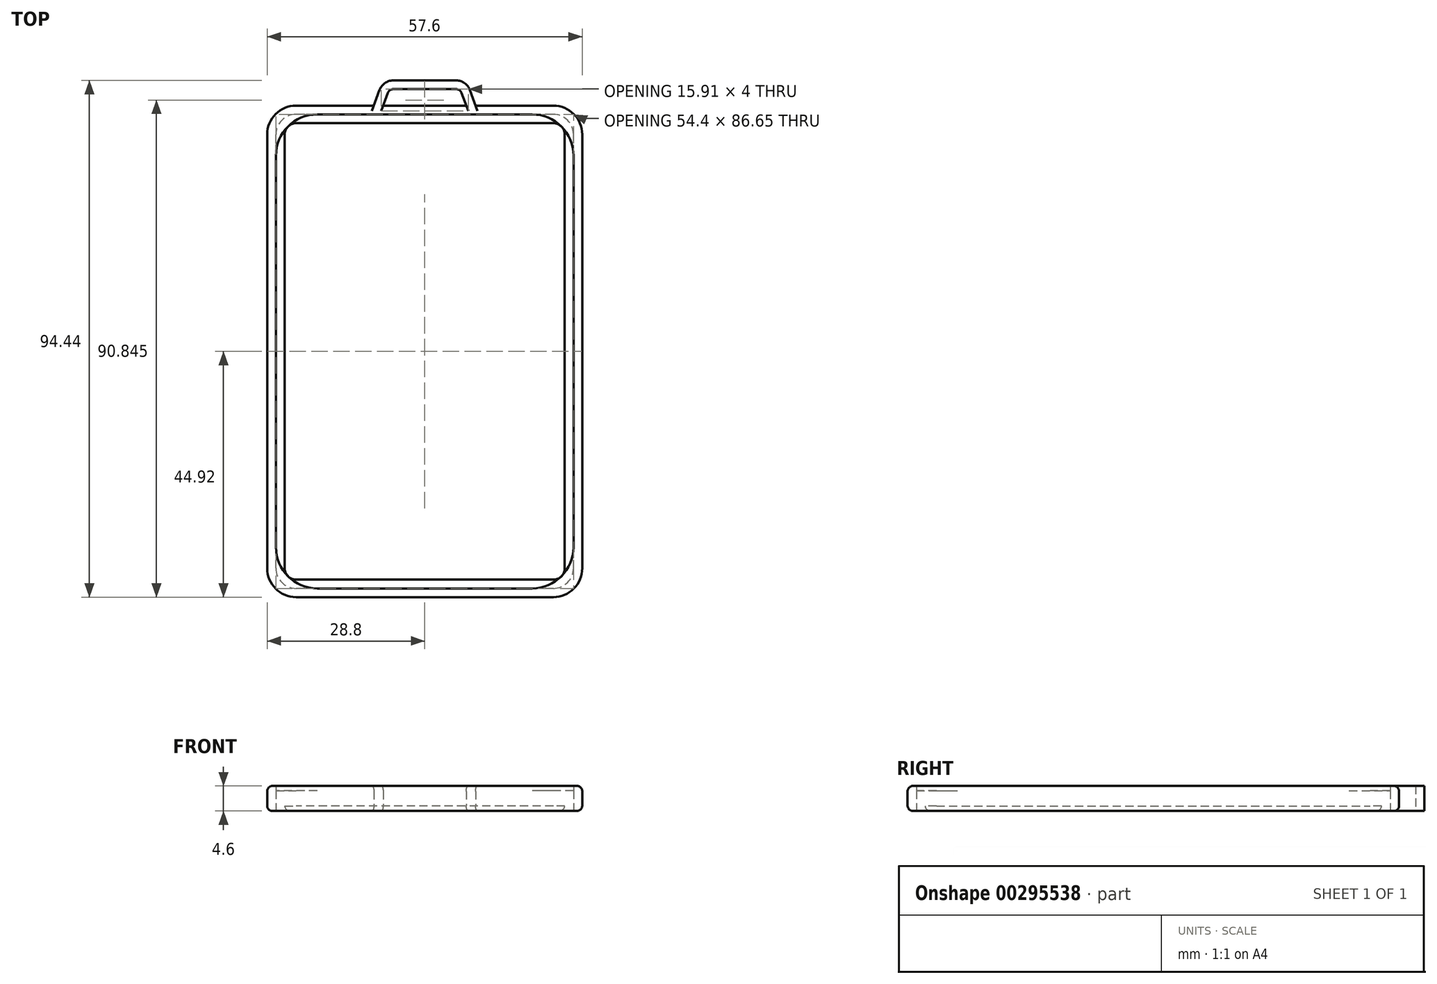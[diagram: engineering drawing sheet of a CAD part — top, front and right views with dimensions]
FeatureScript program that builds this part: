
annotation { "Feature Type Name" : "Feature", "Feature Type Description" : "" }
export const myFeature = defineFeature(function(context is Context, id is Id, definition is map)
    precondition{}
    {
        {
            assignVariable(context, id + "F0", {"variableType" : VariableType.LENGTH, "name" : "BadgeThickness", "lengthValue" : 2.8 * mm});
        }
        {
            var Q0;
            Q0=qCreatedBy(makeId("Top.planeOp"),FACE);
            var sketch = newSketch(context, id + "F1", { "sketchPlane" : qUnion([Q0])});
            skLineSegment(sketch, "E0.bottom", {"start": v(23.52, -43.13) * mm, "end": v(-23.51, -43.13) * mm});
            skLineSegment(sketch, "E0.top", {"start": v(23.51, 43.13) * mm, "end": v(-23.52, 43.13) * mm});
            skLineSegment(sketch, "E0.left", {"start": v(27, -39.64) * mm, "end": v(27, 39.64) * mm});
            skLineSegment(sketch, "E0.right", {"start": v(-27, -39.64) * mm, "end": v(-27, 39.64) * mm, "construction": true});
            skPoint(sketch, "E0.middle", {"position": v(0, 0) * mm});
            skPoint(sketch, "E1.visualSharp", {"position": v(-27, 43.13) * mm});
            skArc(sketch, "E1.filletArc", {"start": v(-23.52, 43.13) * mm, "mid": v(-25.98, 42.1) * mm, "end": v(-27, 39.64) * mm});
            skPoint(sketch, "E2.visualSharp", {"position": v(27, 43.13) * mm});
            skArc(sketch, "E2.filletArc", {"start": v(27, 39.64) * mm, "mid": v(25.98, 42.1) * mm, "end": v(23.51, 43.12) * mm});
            skPoint(sketch, "E3.visualSharp", {"position": v(27, -43.12) * mm});
            skArc(sketch, "E3.filletArc", {"start": v(23.52, -43.12) * mm, "mid": v(25.98, -42.1) * mm, "end": v(27, -39.64) * mm});
            skPoint(sketch, "E4.visualSharp", {"position": v(-27, -43.13) * mm});
            skArc(sketch, "E4.filletArc", {"start": v(-27, -39.64) * mm, "mid": v(-25.98, -42.1) * mm, "end": v(-23.51, -43.13) * mm});
            skArc(sketch, "E5.0", {"start": v(-27.2, -39.64) * mm, "mid": v(-26.12, -42.25) * mm, "end": v(-23.51, -43.33) * mm});
            skLineSegment(sketch, "E5.1", {"start": v(23.52, -43.33) * mm, "end": v(-23.51, -43.33) * mm});
            skLineSegment(sketch, "E5.2", {"start": v(-27.2, -39.64) * mm, "end": v(-27.2, 39.64) * mm});
            skArc(sketch, "E5.3", {"start": v(23.52, -43.32) * mm, "mid": v(26.12, -42.25) * mm, "end": v(27.2, -39.64) * mm});
            skArc(sketch, "E5.4", {"start": v(-23.52, 43.33) * mm, "mid": v(-26.12, 42.25) * mm, "end": v(-27.2, 39.64) * mm});
            skLineSegment(sketch, "E5.5", {"start": v(23.51, 43.33) * mm, "end": v(-23.52, 43.33) * mm});
            skArc(sketch, "E5.6", {"start": v(27.2, 39.64) * mm, "mid": v(26.12, 42.25) * mm, "end": v(23.51, 43.32) * mm});
            skLineSegment(sketch, "E5.7", {"start": v(27.2, -39.64) * mm, "end": v(27.2, 39.64) * mm});
            skArc(sketch, "E6.0", {"start": v(-28.8, -39.64) * mm, "mid": v(-27.25, -43.38) * mm, "end": v(-23.51, -44.92) * mm});
            skLineSegment(sketch, "E6.1", {"start": v(23.52, -44.93) * mm, "end": v(-23.51, -44.93) * mm});
            skLineSegment(sketch, "E6.2", {"start": v(-28.8, -39.64) * mm, "end": v(-28.8, 39.64) * mm});
            skArc(sketch, "E6.3", {"start": v(23.52, -44.92) * mm, "mid": v(27.25, -43.38) * mm, "end": v(28.8, -39.64) * mm});
            skArc(sketch, "E6.4", {"start": v(-23.52, 44.92) * mm, "mid": v(-27.25, 43.38) * mm, "end": v(-28.8, 39.64) * mm});
            skLineSegment(sketch, "E6.5", {"start": v(23.51, 44.93) * mm, "end": v(-23.52, 44.93) * mm});
            skArc(sketch, "E6.6", {"start": v(28.8, 39.64) * mm, "mid": v(27.25, 43.38) * mm, "end": v(23.51, 44.92) * mm});
            skLineSegment(sketch, "E6.7", {"start": v(28.8, -39.64) * mm, "end": v(28.8, 39.64) * mm});
            skSolve(sketch);
        }
        {
            var Q0;
            Q0=makeQuery(id+"F1.imprint","IMPRINT",FACE,{"disambiguationData":[TD([[makeQuery(id+"F1.imprint","IMPRINT",EDGE,{"derivedFrom":sQuery(id+"F1.wireOp",EDGE,"E5.0")}),-1.0]])]});
            extrude(context, id + "F2", {"entities" : qUnion([Q0]), "offsetDistance" : 25 * mm, "depth" : getVariable(context, 'BadgeThickness')});
        }
        {
            var Q0;
            Q0=makeQuery(id+"F2.opExtrude","CAP_FACE",FACE,{"disambiguationData":[OSD([sQuery(id+"F1.wireOp",EDGE,"E5.0"),sQuery(id+"F1.wireOp",EDGE,"E5.1"),sQuery(id+"F1.wireOp",EDGE,"E5.2"),sQuery(id+"F1.wireOp",EDGE,"E5.3"),sQuery(id+"F1.wireOp",EDGE,"E5.4"),sQuery(id+"F1.wireOp",EDGE,"E5.5"),sQuery(id+"F1.wireOp",EDGE,"E5.6"),sQuery(id+"F1.wireOp",EDGE,"E5.7"),sQuery(id+"F1.wireOp",EDGE,"E6.0"),sQuery(id+"F1.wireOp",EDGE,"E6.1"),sQuery(id+"F1.wireOp",EDGE,"E6.2"),sQuery(id+"F1.wireOp",EDGE,"E6.3"),sQuery(id+"F1.wireOp",EDGE,"E6.4"),sQuery(id+"F1.wireOp",EDGE,"E6.5"),sQuery(id+"F1.wireOp",EDGE,"E6.6"),sQuery(id+"F1.wireOp",EDGE,"E6.7")])],"isStart":true});
            var sketch = newSketch(context, id + "F3", { "sketchPlane" : qUnion([Q0])});
            skArc(sketch, "E7.0.0", {"start": v(28.8, 39.64) * mm, "mid": v(27.25, 43.38) * mm, "end": v(23.52, 44.92) * mm});
            skLineSegment(sketch, "E7.0.1", {"start": v(23.52, 44.93) * mm, "end": v(-23.51, 44.93) * mm});
            skArc(sketch, "E7.0.2", {"start": v(-23.51, 44.93) * mm, "mid": v(-27.25, 43.38) * mm, "end": v(-28.8, 39.64) * mm});
            skLineSegment(sketch, "E7.0.3", {"start": v(-28.8, 39.64) * mm, "end": v(-28.8, -39.64) * mm});
            skArc(sketch, "E7.0.4", {"start": v(-28.8, -39.64) * mm, "mid": v(-27.25, -43.38) * mm, "end": v(-23.52, -44.93) * mm});
            skLineSegment(sketch, "E7.0.5", {"start": v(-23.52, -44.93) * mm, "end": v(23.51, -44.93) * mm});
            skArc(sketch, "E7.0.6", {"start": v(23.51, -44.92) * mm, "mid": v(27.25, -43.38) * mm, "end": v(28.8, -39.64) * mm});
            skLineSegment(sketch, "E7.0.7", {"start": v(28.8, -39.64) * mm, "end": v(28.8, 39.64) * mm});
            skArc(sketch, "E8.0", {"start": v(-25.6, 39.64) * mm, "mid": v(-24.99, 41.11) * mm, "end": v(-23.51, 41.73) * mm});
            skLineSegment(sketch, "E8.1", {"start": v(23.51, 41.73) * mm, "end": v(-23.51, 41.73) * mm});
            skLineSegment(sketch, "E8.2", {"start": v(-25.6, 39.64) * mm, "end": v(-25.6, -39.64) * mm});
            skArc(sketch, "E8.3", {"start": v(23.51, 41.72) * mm, "mid": v(24.99, 41.11) * mm, "end": v(25.6, 39.64) * mm});
            skArc(sketch, "E8.4", {"start": v(-23.52, -41.73) * mm, "mid": v(-24.99, -41.11) * mm, "end": v(-25.6, -39.64) * mm});
            skLineSegment(sketch, "E8.5", {"start": v(23.51, -41.73) * mm, "end": v(-23.52, -41.73) * mm});
            skArc(sketch, "E8.6", {"start": v(25.6, -39.64) * mm, "mid": v(24.99, -41.11) * mm, "end": v(23.51, -41.73) * mm});
            skLineSegment(sketch, "E8.7", {"start": v(25.6, 39.64) * mm, "end": v(25.6, -39.64) * mm});
            skSolve(sketch);
        }
        {
            var Q0;
            Q0=makeQuery(id+"F3.imprint","IMPRINT",FACE,{"disambiguationData":[TD([[makeQuery(id+"F3.imprint","IMPRINT",EDGE,{"derivedFrom":sQuery(id+"F3.wireOp",EDGE,"E8.0")}),1.0]])]});
            var Q1;
            Q1=makeQuery(id+"F3.imprint","IMPRINT",FACE,{"disambiguationData":[TD([[makeQuery(id+"F3.imprint","IMPRINT",EDGE,{"derivedFrom":sQuery(id+"F3.wireOp",EDGE,"E7.0.0")}),-1.0]])]});
            extrude(context, id + "F4", {"entities" : qUnion([Q0, Q1]), "operationType" : NewBodyOperationType.ADD, "depth" : 0.9 * mm});
        }
        {
            var Q0;
            Q0=makeQuery(id+"F2.opExtrude","CAP_FACE",FACE,{"disambiguationData":[OSD([sQuery(id+"F1.wireOp",EDGE,"E5.0"),sQuery(id+"F1.wireOp",EDGE,"E5.1"),sQuery(id+"F1.wireOp",EDGE,"E5.2"),sQuery(id+"F1.wireOp",EDGE,"E5.3"),sQuery(id+"F1.wireOp",EDGE,"E5.4"),sQuery(id+"F1.wireOp",EDGE,"E5.5"),sQuery(id+"F1.wireOp",EDGE,"E5.6"),sQuery(id+"F1.wireOp",EDGE,"E5.7"),sQuery(id+"F1.wireOp",EDGE,"E6.0"),sQuery(id+"F1.wireOp",EDGE,"E6.1"),sQuery(id+"F1.wireOp",EDGE,"E6.2"),sQuery(id+"F1.wireOp",EDGE,"E6.3"),sQuery(id+"F1.wireOp",EDGE,"E6.4"),sQuery(id+"F1.wireOp",EDGE,"E6.5"),sQuery(id+"F1.wireOp",EDGE,"E6.6"),sQuery(id+"F1.wireOp",EDGE,"E6.7")])],"isStart":false});
            var sketch = newSketch(context, id + "F5", { "sketchPlane" : qUnion([Q0])});
            skLineSegment(sketch, "E9.0", {"start": v(23.51, 43.33) * mm, "end": v(-23.52, 43.33) * mm});
            skLineSegment(sketch, "E10.0", {"start": v(-27.2, -39.64) * mm, "end": v(-27.2, 39.64) * mm});
            skLineSegment(sketch, "E11.0", {"start": v(27.2, -39.64) * mm, "end": v(27.2, 39.64) * mm});
            skLineSegment(sketch, "E12.0", {"start": v(23.52, -43.33) * mm, "end": v(-23.51, -43.33) * mm});
            skArc(sketch, "E13", {"start": v(-27.2, -35.78) * mm, "mid": v(-24.99, -41.11) * mm, "end": v(-19.65, -43.33) * mm});
            skArc(sketch, "E14", {"start": v(19.65, -43.33) * mm, "mid": v(24.99, -41.11) * mm, "end": v(27.2, -35.78) * mm});
            skArc(sketch, "E15", {"start": v(27.2, 35.78) * mm, "mid": v(24.99, 41.11) * mm, "end": v(19.65, 43.33) * mm});
            skArc(sketch, "E16", {"start": v(-19.65, 43.33) * mm, "mid": v(-24.99, 41.11) * mm, "end": v(-27.2, 35.78) * mm});
            skArc(sketch, "E17.0.0", {"start": v(23.52, -44.92) * mm, "mid": v(27.25, -43.38) * mm, "end": v(28.8, -39.64) * mm});
            skLineSegment(sketch, "E17.0.1", {"start": v(28.8, -39.64) * mm, "end": v(28.8, 39.64) * mm});
            skArc(sketch, "E17.0.2", {"start": v(28.8, 39.64) * mm, "mid": v(27.25, 43.38) * mm, "end": v(23.51, 44.92) * mm});
            skLineSegment(sketch, "E17.0.3", {"start": v(23.51, 44.93) * mm, "end": v(-23.52, 44.93) * mm});
            skArc(sketch, "E17.0.4", {"start": v(-23.52, 44.93) * mm, "mid": v(-27.25, 43.38) * mm, "end": v(-28.8, 39.64) * mm});
            skLineSegment(sketch, "E17.0.5", {"start": v(-28.8, 39.64) * mm, "end": v(-28.8, -39.64) * mm});
            skArc(sketch, "E17.0.6", {"start": v(-28.8, -39.64) * mm, "mid": v(-27.25, -43.38) * mm, "end": v(-23.51, -44.93) * mm});
            skLineSegment(sketch, "E17.0.7", {"start": v(-23.51, -44.93) * mm, "end": v(23.52, -44.93) * mm});
            skSolve(sketch);
        }
        {
            var Q0;
            Q0=makeQuery(id+"F5.imprint","IMPRINT",FACE,{"disambiguationData":[TD([[makeQuery(id+"F5.imprint","IMPRINT",EDGE,{"derivedFrom":sQuery(id+"F5.wireOp",EDGE,"E17.0.0")}),1.0]])]});
            var Q1;
            {var subQ2=sQuery(id+"F5.wireOp",EDGE,"E16");Q1=makeQuery(id+"F5.imprint","IMPRINT",FACE,{"disambiguationData":[TD([[makeQuery(id+"F5.imprint","IMPRINT",EDGE,{"derivedFrom":subQ2}),-1.0]])]});}
            var Q2;
            {var subQ2=sQuery(id+"F5.wireOp",EDGE,"E15");Q2=makeQuery(id+"F5.imprint","IMPRINT",FACE,{"disambiguationData":[TD([[makeQuery(id+"F5.imprint","IMPRINT",EDGE,{"derivedFrom":subQ2}),-1.0]])]});}
            var Q3;
            {var subQ2=sQuery(id+"F5.wireOp",EDGE,"E14");Q3=makeQuery(id+"F5.imprint","IMPRINT",FACE,{"disambiguationData":[TD([[makeQuery(id+"F5.imprint","IMPRINT",EDGE,{"derivedFrom":subQ2}),-1.0]])]});}
            var Q4;
            {var subQ2=sQuery(id+"F5.wireOp",EDGE,"E13");Q4=makeQuery(id+"F5.imprint","IMPRINT",FACE,{"disambiguationData":[TD([[makeQuery(id+"F5.imprint","IMPRINT",EDGE,{"derivedFrom":subQ2}),-1.0]])]});}
            extrude(context, id + "F6", {"entities" : qUnion([Q0, Q1, Q2, Q3, Q4]), "operationType" : NewBodyOperationType.ADD, "depth" : 0.9 * mm});
        }
        {
            var Q0;
            Q0=qCreatedBy(makeId("Top.planeOp"),FACE);
            var sketch = newSketch(context, id + "F7", { "sketchPlane" : qUnion([Q0])});
            skLineSegment(sketch, "E18", {"start": v(-7.6, 44.93) * mm, "end": v(-6.74, 47.27) * mm});
            skLineSegment(sketch, "E19", {"start": v(-5.8, 47.93) * mm, "end": v(5.8, 47.93) * mm});
            skLineSegment(sketch, "E20", {"start": v(6.74, 47.27) * mm, "end": v(7.6, 44.93) * mm});
            skLineSegment(sketch, "E21", {"start": v(0, 0) * mm, "end": v(0, 7.2) * mm, "construction": true});
            skPoint(sketch, "E22.visualSharp", {"position": v(-6.5, 47.93) * mm});
            skArc(sketch, "E22.filletArc", {"start": v(-5.8, 47.93) * mm, "mid": v(-6.37, 47.74) * mm, "end": v(-6.74, 47.27) * mm});
            skPoint(sketch, "E23.visualSharp", {"position": v(6.5, 47.93) * mm});
            skArc(sketch, "E23.filletArc", {"start": v(6.74, 47.27) * mm, "mid": v(6.37, 47.74) * mm, "end": v(5.8, 47.93) * mm});
            skLineSegment(sketch, "E24.0", {"start": v(8.24, 47.81) * mm, "end": v(9.3, 44.93) * mm});
            skLineSegment(sketch, "E24.1", {"start": v(-9.3, 44.93) * mm, "end": v(-8.24, 47.81) * mm});
            skArc(sketch, "E24.2", {"start": v(-5.8, 49.53) * mm, "mid": v(-7.3, 49.05) * mm, "end": v(-8.24, 47.81) * mm});
            skLineSegment(sketch, "E24.3", {"start": v(-5.8, 49.53) * mm, "end": v(5.8, 49.53) * mm});
            skArc(sketch, "E24.4", {"start": v(8.24, 47.81) * mm, "mid": v(7.3, 49.05) * mm, "end": v(5.8, 49.53) * mm});
            skLineSegment(sketch, "E25", {"start": v(9.3, 44.93) * mm, "end": v(7.6, 44.93) * mm});
            skLineSegment(sketch, "E26", {"start": v(-7.6, 44.93) * mm, "end": v(-9.3, 44.93) * mm});
            skSolve(sketch);
        }
        {
            var Q0;
            Q0 = qSketchRegion(id + "F7", true);
            var Q1;
            Q1=makeQuery(id+"F6.opExtrude","CAP_FACE",FACE,{"disambiguationData":[OSD([sQuery(id+"F5.wireOp",EDGE,"E9.0"),sQuery(id+"F5.wireOp",EDGE,"E10.0"),sQuery(id+"F5.wireOp",EDGE,"E11.0"),sQuery(id+"F5.wireOp",EDGE,"E12.0"),sQuery(id+"F5.wireOp",EDGE,"E13"),sQuery(id+"F5.wireOp",EDGE,"E14"),sQuery(id+"F5.wireOp",EDGE,"E15"),sQuery(id+"F5.wireOp",EDGE,"E16"),sQuery(id+"F5.wireOp",EDGE,"E17.0.0"),sQuery(id+"F5.wireOp",EDGE,"E17.0.1"),sQuery(id+"F5.wireOp",EDGE,"E17.0.2"),sQuery(id+"F5.wireOp",EDGE,"E17.0.3"),sQuery(id+"F5.wireOp",EDGE,"E17.0.4"),sQuery(id+"F5.wireOp",EDGE,"E17.0.5"),sQuery(id+"F5.wireOp",EDGE,"E17.0.6"),sQuery(id+"F5.wireOp",EDGE,"E17.0.7")])],"isStart":false});
            var Q2;
            Q2=makeQuery(id+"F4.opExtrude","CAP_FACE",FACE,{"disambiguationData":[OSD([sQuery(id+"F3.wireOp",EDGE,"E7.0.0"),sQuery(id+"F3.wireOp",EDGE,"E7.0.1"),sQuery(id+"F3.wireOp",EDGE,"E7.0.2"),sQuery(id+"F3.wireOp",EDGE,"E7.0.3"),sQuery(id+"F3.wireOp",EDGE,"E7.0.4"),sQuery(id+"F3.wireOp",EDGE,"E7.0.5"),sQuery(id+"F3.wireOp",EDGE,"E7.0.6"),sQuery(id+"F3.wireOp",EDGE,"E7.0.7"),sQuery(id+"F3.wireOp",EDGE,"E8.0"),sQuery(id+"F3.wireOp",EDGE,"E8.1"),sQuery(id+"F3.wireOp",EDGE,"E8.2"),sQuery(id+"F3.wireOp",EDGE,"E8.3"),sQuery(id+"F3.wireOp",EDGE,"E8.4"),sQuery(id+"F3.wireOp",EDGE,"E8.5"),sQuery(id+"F3.wireOp",EDGE,"E8.6"),sQuery(id+"F3.wireOp",EDGE,"E8.7")])],"isStart":false});
            extrude(context, id + "F8", {"entities" : qUnion([Q0]), "operationType" : NewBodyOperationType.ADD, "endBound" : BoundingType.UP_TO_SURFACE, "endBoundEntityFace" : qUnion([Q1]), "depth" : 25 * mm, "hasSecondDirection" : true, "secondDirectionBound" : SecondDirectionBoundingType.UP_TO_SURFACE, "secondDirectionOppositeDirection" : true, "secondDirectionBoundEntityFace" : qUnion([Q2]), "secondDirectionDepth" : 25 * mm});
        }
        {
            var Q0;
            Q0=makeQuery(id+"F6.opExtrude","CAP_EDGE",EDGE,{"disambiguationData":[OSD([sQuery(id+"F5.wireOp",EDGE,"E17.0.5")])],"isStart":false});
            var Q1;
            Q1=makeQuery(id+"F4.opExtrude","CAP_EDGE",EDGE,{"disambiguationData":[OSD([sQuery(id+"F3.wireOp",EDGE,"E7.0.3")])],"isStart":false});
            var Q2;
            Q2=makeQuery(id+"F8.opExtrude","TWEAK_EDGE",EDGE,{"derivedFrom":[makeQuery(id+"F6.opExtrude","CAP_FACE",FACE,{"disambiguationData":[OSD([sQuery(id+"F5.wireOp",EDGE,"E9.0"),sQuery(id+"F5.wireOp",EDGE,"E10.0"),sQuery(id+"F5.wireOp",EDGE,"E11.0"),sQuery(id+"F5.wireOp",EDGE,"E12.0"),sQuery(id+"F5.wireOp",EDGE,"E13"),sQuery(id+"F5.wireOp",EDGE,"E14"),sQuery(id+"F5.wireOp",EDGE,"E15"),sQuery(id+"F5.wireOp",EDGE,"E16"),sQuery(id+"F5.wireOp",EDGE,"E17.0.0"),sQuery(id+"F5.wireOp",EDGE,"E17.0.1"),sQuery(id+"F5.wireOp",EDGE,"E17.0.2"),sQuery(id+"F5.wireOp",EDGE,"E17.0.3"),sQuery(id+"F5.wireOp",EDGE,"E17.0.4"),sQuery(id+"F5.wireOp",EDGE,"E17.0.5"),sQuery(id+"F5.wireOp",EDGE,"E17.0.6"),sQuery(id+"F5.wireOp",EDGE,"E17.0.7")])],"isStart":false}),makeQuery(id+"F7.imprint","IMPRINT",EDGE,{"derivedFrom":sQuery(id+"F7.wireOp",EDGE,"E18")})]});
            var Q3;
            Q3=makeQuery(id+"F8.opExtrude","TWEAK_EDGE",EDGE,{"derivedFrom":[makeQuery(id+"F4.opExtrude","CAP_FACE",FACE,{"disambiguationData":[OSD([sQuery(id+"F3.wireOp",EDGE,"E7.0.0"),sQuery(id+"F3.wireOp",EDGE,"E7.0.1"),sQuery(id+"F3.wireOp",EDGE,"E7.0.2"),sQuery(id+"F3.wireOp",EDGE,"E7.0.3"),sQuery(id+"F3.wireOp",EDGE,"E7.0.4"),sQuery(id+"F3.wireOp",EDGE,"E7.0.5"),sQuery(id+"F3.wireOp",EDGE,"E7.0.6"),sQuery(id+"F3.wireOp",EDGE,"E7.0.7"),sQuery(id+"F3.wireOp",EDGE,"E8.0"),sQuery(id+"F3.wireOp",EDGE,"E8.1"),sQuery(id+"F3.wireOp",EDGE,"E8.2"),sQuery(id+"F3.wireOp",EDGE,"E8.3"),sQuery(id+"F3.wireOp",EDGE,"E8.4"),sQuery(id+"F3.wireOp",EDGE,"E8.5"),sQuery(id+"F3.wireOp",EDGE,"E8.6"),sQuery(id+"F3.wireOp",EDGE,"E8.7")])],"isStart":false}),makeQuery(id+"F7.imprint","IMPRINT",EDGE,{"derivedFrom":sQuery(id+"F7.wireOp",EDGE,"E24.3")})]});
            var Q4;
            Q4=makeQuery(id+"F8.opExtrude","TWEAK_EDGE",EDGE,{"derivedFrom":[makeQuery(id+"F6.opExtrude","CAP_FACE",FACE,{"disambiguationData":[OSD([sQuery(id+"F5.wireOp",EDGE,"E9.0"),sQuery(id+"F5.wireOp",EDGE,"E10.0"),sQuery(id+"F5.wireOp",EDGE,"E11.0"),sQuery(id+"F5.wireOp",EDGE,"E12.0"),sQuery(id+"F5.wireOp",EDGE,"E13"),sQuery(id+"F5.wireOp",EDGE,"E14"),sQuery(id+"F5.wireOp",EDGE,"E15"),sQuery(id+"F5.wireOp",EDGE,"E16"),sQuery(id+"F5.wireOp",EDGE,"E17.0.0"),sQuery(id+"F5.wireOp",EDGE,"E17.0.1"),sQuery(id+"F5.wireOp",EDGE,"E17.0.2"),sQuery(id+"F5.wireOp",EDGE,"E17.0.3"),sQuery(id+"F5.wireOp",EDGE,"E17.0.4"),sQuery(id+"F5.wireOp",EDGE,"E17.0.5"),sQuery(id+"F5.wireOp",EDGE,"E17.0.6"),sQuery(id+"F5.wireOp",EDGE,"E17.0.7")])],"isStart":false}),makeQuery(id+"F7.imprint","IMPRINT",EDGE,{"derivedFrom":sQuery(id+"F7.wireOp",EDGE,"E24.3")})]});
            var Q5;
            {var subQ0=sQuery(id+"F3.wireOp",EDGE,"E7.0.5");Q5=makeQuery(id+"F8.boolean.opBoolean","SPLIT",EDGE,{"disambiguationData":[TD([makeQuery(id+"F8.opExtrude","SWEPT_FACE",FACE,{"disambiguationData":[OSD([sQuery(id+"F7.wireOp",EDGE,"E18")])]})])],"derivedFrom":makeQuery(id+"F4.opExtrude","CAP_EDGE",EDGE,{"disambiguationData":[OSD([subQ0])],"isStart":false})});}
            var Q6;
            {var subQ4=sQuery(id+"F5.wireOp",EDGE,"E17.0.3");Q6=makeQuery(id+"F8.boolean.opBoolean","SPLIT",EDGE,{"disambiguationData":[TD([makeQuery(id+"F8.opExtrude","SWEPT_FACE",FACE,{"disambiguationData":[OSD([sQuery(id+"F7.wireOp",EDGE,"E18")])]})])],"derivedFrom":makeQuery(id+"F6.opExtrude","CAP_EDGE",EDGE,{"disambiguationData":[OSD([subQ4])],"isStart":false})});}
            var Q7;
            Q7=makeQuery(id+"F8.opExtrude","TWEAK_EDGE",EDGE,{"derivedFrom":[makeQuery(id+"F4.opExtrude","CAP_FACE",FACE,{"disambiguationData":[OSD([sQuery(id+"F3.wireOp",EDGE,"E7.0.0"),sQuery(id+"F3.wireOp",EDGE,"E7.0.1"),sQuery(id+"F3.wireOp",EDGE,"E7.0.2"),sQuery(id+"F3.wireOp",EDGE,"E7.0.3"),sQuery(id+"F3.wireOp",EDGE,"E7.0.4"),sQuery(id+"F3.wireOp",EDGE,"E7.0.5"),sQuery(id+"F3.wireOp",EDGE,"E7.0.6"),sQuery(id+"F3.wireOp",EDGE,"E7.0.7"),sQuery(id+"F3.wireOp",EDGE,"E8.0"),sQuery(id+"F3.wireOp",EDGE,"E8.1"),sQuery(id+"F3.wireOp",EDGE,"E8.2"),sQuery(id+"F3.wireOp",EDGE,"E8.3"),sQuery(id+"F3.wireOp",EDGE,"E8.4"),sQuery(id+"F3.wireOp",EDGE,"E8.5"),sQuery(id+"F3.wireOp",EDGE,"E8.6"),sQuery(id+"F3.wireOp",EDGE,"E8.7")])],"isStart":false}),makeQuery(id+"F7.imprint","IMPRINT",EDGE,{"derivedFrom":sQuery(id+"F7.wireOp",EDGE,"E19")})]});
            var Q8;
            Q8=makeQuery(id+"F4.opExtrude","CAP_EDGE",EDGE,{"disambiguationData":[OSD([sQuery(id+"F3.wireOp",EDGE,"E8.2")])],"isStart":false});
            fillet(context, id + "F9", {"entities" : qUnion([Q0, Q1, Q2, Q3, Q4, Q5, Q6, Q7, Q8]), "radius" : 1 * mm, "tangentPropagation" : true, "allowEdgeOverflow" : false});
        }
    });
